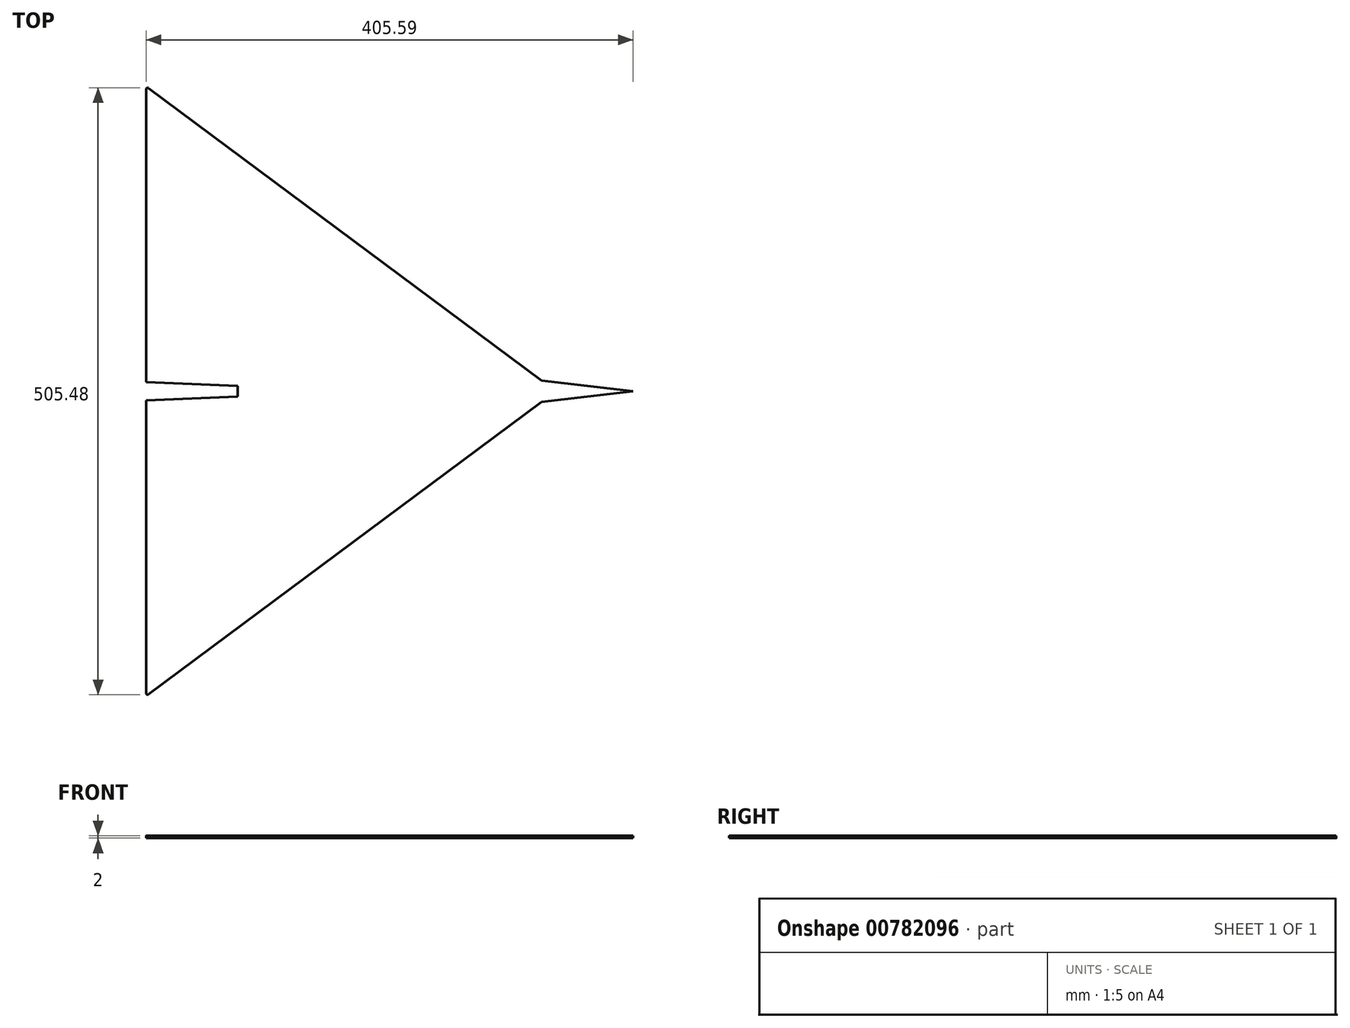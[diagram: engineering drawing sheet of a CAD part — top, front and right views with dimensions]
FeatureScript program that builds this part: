
annotation { "Feature Type Name" : "Feature", "Feature Type Description" : "" }
export const myFeature = defineFeature(function(context is Context, id is Id, definition is map)
    precondition{}
    {
        {
            var Q0;
            Q0=qCreatedBy(makeId("Top.planeOp"),FACE);
            var sketch = newSketch(context, id + "F0", { "sketchPlane" : qUnion([Q0])});
            skLineSegment(sketch, "E0", {"start": v(0, 8.89) * mm, "end": v(76.2, 0) * mm});
            skLineSegment(sketch, "E1", {"start": v(76.2, 0) * mm, "end": v(0, 0) * mm, "construction": true});
            skLineSegment(sketch, "E2", {"start": v(-327.36, 252.5) * mm, "end": v(0, 8.89) * mm});
            skLineSegment(sketch, "E3", {"start": v(-329.39, 251.47) * mm, "end": v(-329.39, 7.62) * mm});
            skLineSegment(sketch, "E4", {"start": v(-329.39, 7.62) * mm, "end": v(-253.19, 4.44) * mm});
            skLineSegment(sketch, "E5", {"start": v(-253.19, 4.44) * mm, "end": v(-253.19, 0) * mm});
            skLineSegment(sketch, "E6.MirrorCS", {"start": v(-253.19, -4.45) * mm, "end": v(-253.19, 0) * mm});
            skLineSegment(sketch, "E7.MirrorCS", {"start": v(-329.39, -7.62) * mm, "end": v(-253.19, -4.45) * mm});
            skLineSegment(sketch, "E8.MirrorCS", {"start": v(-329.39, -251.47) * mm, "end": v(-329.39, -7.62) * mm});
            skLineSegment(sketch, "E9.MirrorCS", {"start": v(-327.36, -252.5) * mm, "end": v(0, -8.89) * mm});
            skLineSegment(sketch, "E10.MirrorCS", {"start": v(0, -8.89) * mm, "end": v(76.2, 0) * mm});
            skPoint(sketch, "E11.visualSharp", {"position": v(-329.39, -254) * mm});
            skArc(sketch, "E11.filletArc", {"start": v(-329.39, -251.47) * mm, "mid": v(-328.69, -252.6) * mm, "end": v(-327.36, -252.5) * mm});
            skPoint(sketch, "E12.visualSharp", {"position": v(-329.39, 254) * mm});
            skArc(sketch, "E12.filletArc", {"start": v(-327.36, 252.5) * mm, "mid": v(-328.69, 252.6) * mm, "end": v(-329.39, 251.47) * mm});
            skSolve(sketch);
        }
        {
            var Q0;
            Q0=makeQuery(id+"F0.imprint","IMPRINT",FACE,{"disambiguationData":[TD([[makeQuery(id+"F0.imprint","IMPRINT",EDGE,{"derivedFrom":sQuery(id+"F0.wireOp",EDGE,"E0")}),-1.0]])]});
            extrude(context, id + "F1", {"entities" : qUnion([Q0]), "depth" : 2 * mm, "offsetDistance" : 25.4 * mm});
        }
    });
